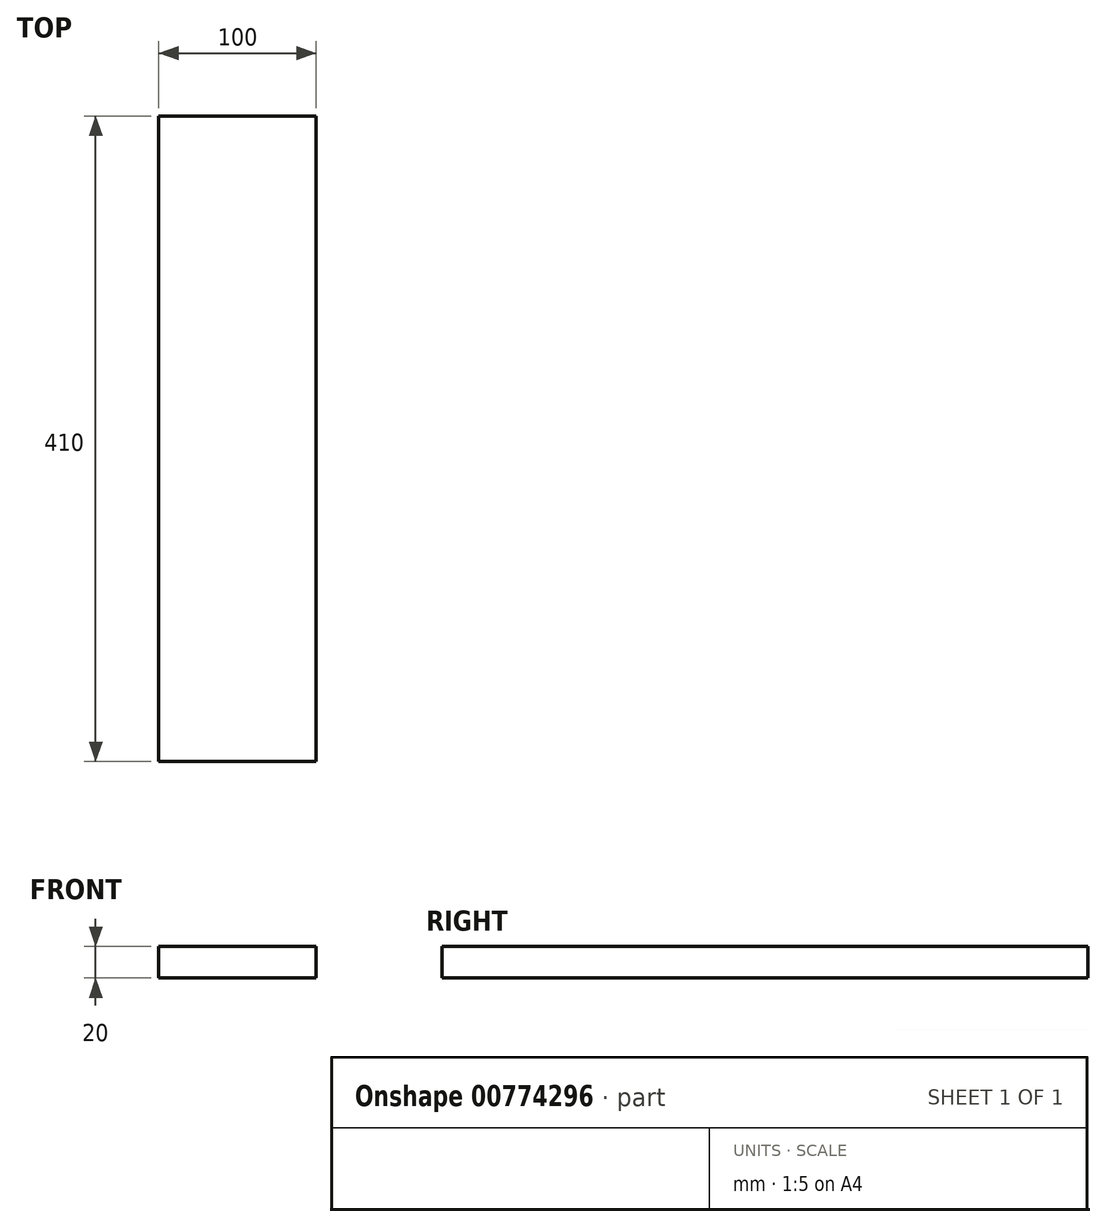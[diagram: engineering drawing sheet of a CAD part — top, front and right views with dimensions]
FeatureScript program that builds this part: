
annotation { "Feature Type Name" : "Feature", "Feature Type Description" : "" }
export const myFeature = defineFeature(function(context is Context, id is Id, definition is map)
    precondition{}
    {
        {
            var Q0;
            Q0=qCreatedBy(makeId("Top.planeOp"),FACE);
            var sketch = newSketch(context, id + "F0", { "sketchPlane" : qUnion([Q0])});
            skLineSegment(sketch, "E0", {"start": v(-88.1, 50) * mm, "end": v(11.9, 50) * mm});
            skLineSegment(sketch, "E1", {"start": v(11.9, 50) * mm, "end": v(11.9, 460) * mm});
            skLineSegment(sketch, "E2", {"start": v(-88.1, 50) * mm, "end": v(-88.1, 460) * mm});
            skLineSegment(sketch, "E3", {"start": v(-88.1, 460) * mm, "end": v(11.9, 460) * mm});
            skSolve(sketch);
        }
        {
            var Q0;
            Q0 = qSketchRegion(id + "F0", true);
            extrude(context, id + "F1", {"entities" : qUnion([Q0]), "depth" : 20 * mm, "offsetDistance" : 25 * mm});
        }
        {
            var Q0;
            Q0=makeQuery(id+"F1.opExtrude","CAP_FACE",FACE,{"disambiguationData":[OSD([sQuery(id+"F0.wireOp",EDGE,"E0"),sQuery(id+"F0.wireOp",EDGE,"E1"),sQuery(id+"F0.wireOp",EDGE,"E2"),sQuery(id+"F0.wireOp",EDGE,"E3")])],"isStart":false});
            var sketch = newSketch(context, id + "F2", { "sketchPlane" : qUnion([Q0])});
            skLineSegment(sketch, "E4", {"start": v(-38.1, 50) * mm, "end": v(-38.1, 460) * mm, "construction": true});
            skLineSegment(sketch, "E5", {"start": v(-88.1, 367) * mm, "end": v(11.9, 367) * mm});
            skLineSegment(sketch, "E6", {"start": v(-88.1, 111) * mm, "end": v(11.9, 111) * mm});
            skLineSegment(sketch, "E7", {"start": v(11.9, 231) * mm, "end": v(-88.1, 231) * mm});
            skLineSegment(sketch, "E8", {"start": v(11.9, 367) * mm, "end": v(11.9, 231) * mm});
            skLineSegment(sketch, "E9.0", {"start": v(-1.1, 367) * mm, "end": v(-1.1, 231) * mm});
            skPoint(sketch, "E10", {"position": v(-1.1, 299) * mm});
            skPoint(sketch, "E11", {"position": v(-38.1, 367) * mm});
            skPoint(sketch, "E12", {"position": v(-38.1, 231) * mm});
            skPoint(sketch, "E13", {"position": v(-38.1, 111) * mm});
            skSolve(sketch);
        }
    });
